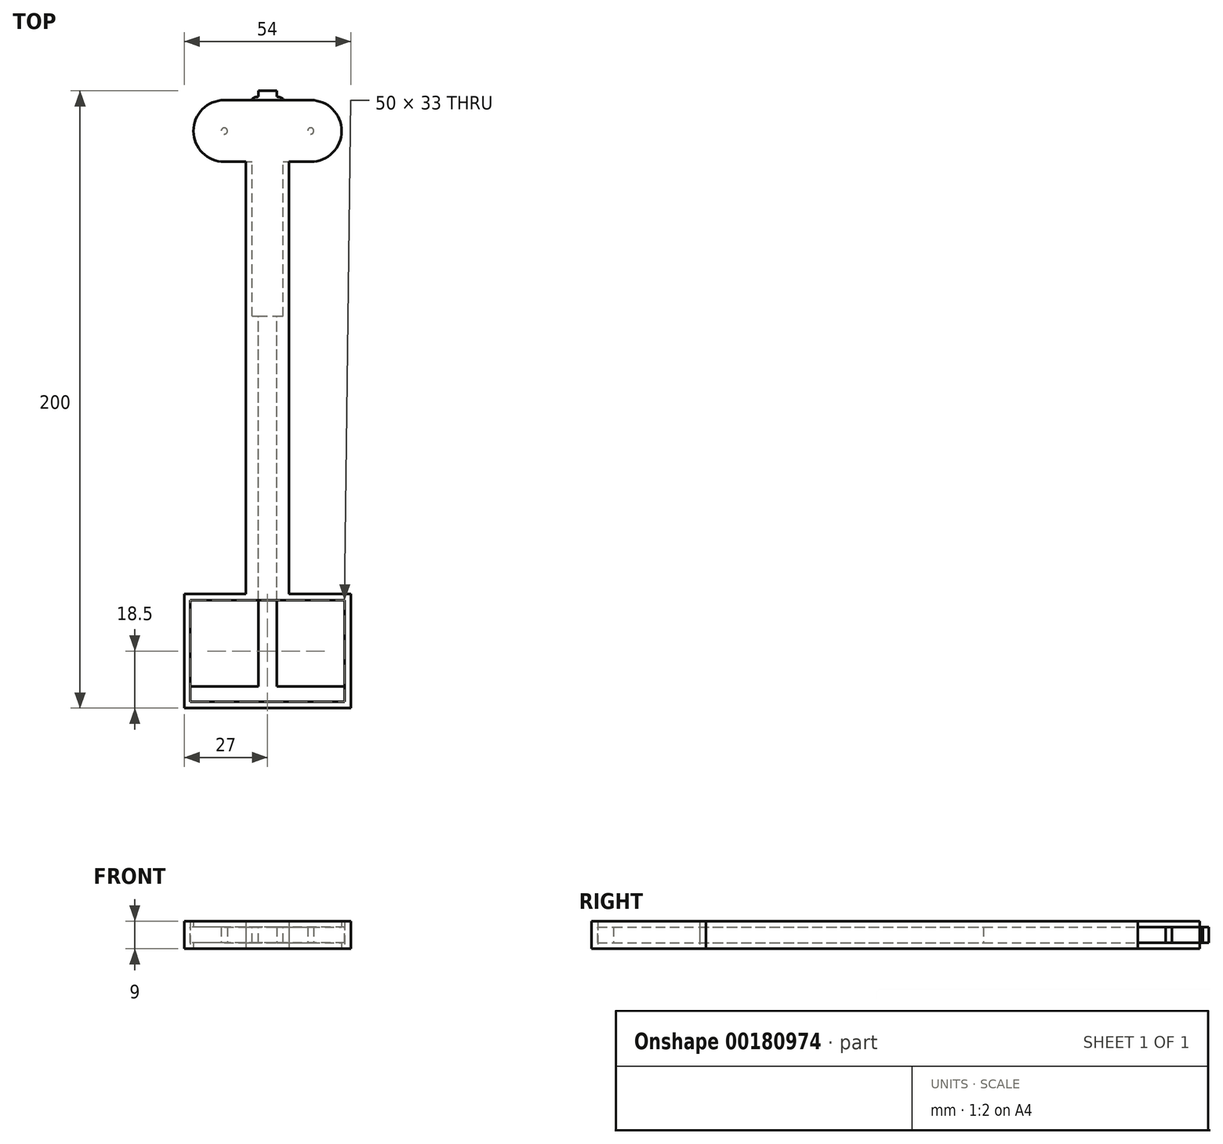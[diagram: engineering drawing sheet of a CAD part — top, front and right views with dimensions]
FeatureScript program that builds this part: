
annotation { "Feature Type Name" : "Feature", "Feature Type Description" : "" }
export const myFeature = defineFeature(function(context is Context, id is Id, definition is map)
    precondition{}
    {
        {
            var Q0;
            Q0=qCreatedBy(makeId("Top.planeOp"),FACE);
            var sketch = newSketch(context, id + "F0", { "sketchPlane" : qUnion([Q0])});
            skLineSegment(sketch, "E0.bottom", {"start": v(0, -180) * mm, "end": v(3, -180) * mm});
            skLineSegment(sketch, "E0.top", {"start": v(0, 13) * mm, "end": v(3, 13) * mm});
            skLineSegment(sketch, "E0.left", {"start": v(0, -180) * mm, "end": v(0, 13) * mm});
            skLineSegment(sketch, "E0.right", {"start": v(3, -180) * mm, "end": v(3, 13) * mm});
            skLineSegment(sketch, "E1", {"start": v(0, 10) * mm, "end": v(3, 10) * mm, "construction": true});
            skArc(sketch, "E2", {"start": v(3, 11.09) * mm, "mid": v(4.04, 10.94) * mm, "end": v(5, 10.5) * mm});
            skLineSegment(sketch, "E3", {"start": v(5, 10.5) * mm, "end": v(5, 10) * mm});
            skArc(sketch, "E4.MirrorCS", {"start": v(3, 8.91) * mm, "mid": v(4.04, 9.06) * mm, "end": v(5, 9.5) * mm});
            skLineSegment(sketch, "E5.MirrorCS", {"start": v(5, 9.5) * mm, "end": v(5, 10) * mm});
            skArc(sketch, "E6.1.0.0", {"start": v(3, 7.89) * mm, "mid": v(4.04, 7.74) * mm, "end": v(5, 7.3) * mm});
            skLineSegment(sketch, "E6.1.0.1", {"start": v(5, 7.3) * mm, "end": v(5, 6.8) * mm});
            skLineSegment(sketch, "E6.1.0.2", {"start": v(5, 6.3) * mm, "end": v(5, 6.8) * mm});
            skArc(sketch, "E6.1.0.3", {"start": v(3, 5.71) * mm, "mid": v(4.04, 5.86) * mm, "end": v(5, 6.3) * mm});
            skArc(sketch, "E6.2.0.0", {"start": v(3, 4.69) * mm, "mid": v(4.04, 4.54) * mm, "end": v(5, 4.1) * mm});
            skLineSegment(sketch, "E6.2.0.1", {"start": v(5, 4.1) * mm, "end": v(5, 3.6) * mm});
            skLineSegment(sketch, "E6.2.0.2", {"start": v(5, 3.1) * mm, "end": v(5, 3.6) * mm});
            skArc(sketch, "E6.2.0.3", {"start": v(3, 2.51) * mm, "mid": v(4.04, 2.66) * mm, "end": v(5, 3.1) * mm});
            skLineSegment(sketch, "E6.direction1", {"start": v(3, 7.39) * mm, "end": v(3, 4.19) * mm, "construction": true});
            skArc(sketch, "E7.0.3.0", {"start": v(3, 1.49) * mm, "mid": v(4.04, 1.34) * mm, "end": v(5, 0.9) * mm});
            skLineSegment(sketch, "E7.4.3.0", {"start": v(5, 0.9) * mm, "end": v(5, 0.4) * mm});
            skLineSegment(sketch, "E7.7.3.0", {"start": v(5, -0.1) * mm, "end": v(5, 0.4) * mm});
            skArc(sketch, "E7.10.3.0", {"start": v(3, -0.69) * mm, "mid": v(4.04, -0.54) * mm, "end": v(5, -0.1) * mm});
            skArc(sketch, "E7.0.4.0", {"start": v(3, -1.71) * mm, "mid": v(4.04, -1.86) * mm, "end": v(5, -2.3) * mm});
            skLineSegment(sketch, "E7.4.4.0", {"start": v(5, -2.3) * mm, "end": v(5, -2.8) * mm});
            skLineSegment(sketch, "E7.7.4.0", {"start": v(5, -3.3) * mm, "end": v(5, -2.8) * mm});
            skArc(sketch, "E7.10.4.0", {"start": v(3, -3.89) * mm, "mid": v(4.04, -3.74) * mm, "end": v(5, -3.3) * mm});
            skArc(sketch, "E7.0.5.0", {"start": v(3, -4.91) * mm, "mid": v(4.04, -5.06) * mm, "end": v(5, -5.5) * mm});
            skLineSegment(sketch, "E7.4.5.0", {"start": v(5, -5.5) * mm, "end": v(5, -6) * mm});
            skLineSegment(sketch, "E7.7.5.0", {"start": v(5, -6.5) * mm, "end": v(5, -6) * mm});
            skArc(sketch, "E7.10.5.0", {"start": v(3, -7.09) * mm, "mid": v(4.04, -6.94) * mm, "end": v(5, -6.5) * mm});
            skArc(sketch, "E7.0.6.0", {"start": v(3, -8.11) * mm, "mid": v(4.04, -8.26) * mm, "end": v(5, -8.7) * mm});
            skLineSegment(sketch, "E7.4.6.0", {"start": v(5, -8.7) * mm, "end": v(5, -9.2) * mm});
            skLineSegment(sketch, "E7.7.6.0", {"start": v(5, -9.7) * mm, "end": v(5, -9.2) * mm});
            skArc(sketch, "E7.10.6.0", {"start": v(3, -10.29) * mm, "mid": v(4.04, -10.14) * mm, "end": v(5, -9.7) * mm});
            skArc(sketch, "E7.0.7.0", {"start": v(3, -11.31) * mm, "mid": v(4.04, -11.46) * mm, "end": v(5, -11.9) * mm});
            skLineSegment(sketch, "E7.4.7.0", {"start": v(5, -11.9) * mm, "end": v(5, -12.4) * mm});
            skLineSegment(sketch, "E7.7.7.0", {"start": v(5, -12.9) * mm, "end": v(5, -12.4) * mm});
            skArc(sketch, "E7.10.7.0", {"start": v(3, -13.49) * mm, "mid": v(4.04, -13.34) * mm, "end": v(5, -12.9) * mm});
            skArc(sketch, "E7.0.8.0", {"start": v(3, -14.51) * mm, "mid": v(4.04, -14.66) * mm, "end": v(5, -15.1) * mm});
            skLineSegment(sketch, "E7.4.8.0", {"start": v(5, -15.1) * mm, "end": v(5, -15.6) * mm});
            skLineSegment(sketch, "E7.7.8.0", {"start": v(5, -16.1) * mm, "end": v(5, -15.6) * mm});
            skArc(sketch, "E7.10.8.0", {"start": v(3, -16.69) * mm, "mid": v(4.04, -16.54) * mm, "end": v(5, -16.1) * mm});
            skArc(sketch, "E7.0.9.0", {"start": v(3, -17.71) * mm, "mid": v(4.04, -17.86) * mm, "end": v(5, -18.3) * mm});
            skLineSegment(sketch, "E7.4.9.0", {"start": v(5, -18.3) * mm, "end": v(5, -18.8) * mm});
            skLineSegment(sketch, "E7.7.9.0", {"start": v(5, -19.3) * mm, "end": v(5, -18.8) * mm});
            skArc(sketch, "E7.10.9.0", {"start": v(3, -19.89) * mm, "mid": v(4.04, -19.74) * mm, "end": v(5, -19.3) * mm});
            skArc(sketch, "E7.0.10.0", {"start": v(3, -20.91) * mm, "mid": v(4.04, -21.06) * mm, "end": v(5, -21.5) * mm});
            skLineSegment(sketch, "E7.4.10.0", {"start": v(5, -21.5) * mm, "end": v(5, -22) * mm});
            skLineSegment(sketch, "E7.7.10.0", {"start": v(5, -22.5) * mm, "end": v(5, -22) * mm});
            skArc(sketch, "E7.10.10.0", {"start": v(3, -23.09) * mm, "mid": v(4.04, -22.94) * mm, "end": v(5, -22.5) * mm});
            skArc(sketch, "E7.0.11.0", {"start": v(3, -24.11) * mm, "mid": v(4.04, -24.26) * mm, "end": v(5, -24.7) * mm});
            skLineSegment(sketch, "E7.4.11.0", {"start": v(5, -24.7) * mm, "end": v(5, -25.2) * mm});
            skLineSegment(sketch, "E7.7.11.0", {"start": v(5, -25.7) * mm, "end": v(5, -25.2) * mm});
            skArc(sketch, "E7.10.11.0", {"start": v(3, -26.29) * mm, "mid": v(4.04, -26.14) * mm, "end": v(5, -25.7) * mm});
            skArc(sketch, "E7.0.12.0", {"start": v(3, -27.31) * mm, "mid": v(4.04, -27.46) * mm, "end": v(5, -27.9) * mm});
            skLineSegment(sketch, "E7.4.12.0", {"start": v(5, -27.9) * mm, "end": v(5, -28.4) * mm});
            skLineSegment(sketch, "E7.7.12.0", {"start": v(5, -28.9) * mm, "end": v(5, -28.4) * mm});
            skArc(sketch, "E7.10.12.0", {"start": v(3, -29.49) * mm, "mid": v(4.04, -29.34) * mm, "end": v(5, -28.9) * mm});
            skArc(sketch, "E7.0.13.0", {"start": v(3, -30.51) * mm, "mid": v(4.04, -30.66) * mm, "end": v(5, -31.1) * mm});
            skLineSegment(sketch, "E7.4.13.0", {"start": v(5, -31.1) * mm, "end": v(5, -31.6) * mm});
            skLineSegment(sketch, "E7.7.13.0", {"start": v(5, -32.1) * mm, "end": v(5, -31.6) * mm});
            skArc(sketch, "E7.10.13.0", {"start": v(3, -32.69) * mm, "mid": v(4.04, -32.54) * mm, "end": v(5, -32.1) * mm});
            skArc(sketch, "E7.0.14.0", {"start": v(3, -33.71) * mm, "mid": v(4.04, -33.86) * mm, "end": v(5, -34.3) * mm});
            skLineSegment(sketch, "E7.4.14.0", {"start": v(5, -34.3) * mm, "end": v(5, -34.8) * mm});
            skLineSegment(sketch, "E7.7.14.0", {"start": v(5, -35.3) * mm, "end": v(5, -34.8) * mm});
            skArc(sketch, "E7.10.14.0", {"start": v(3, -35.89) * mm, "mid": v(4.04, -35.74) * mm, "end": v(5, -35.3) * mm});
            skArc(sketch, "E7.0.15.0", {"start": v(3, -36.91) * mm, "mid": v(4.04, -37.06) * mm, "end": v(5, -37.5) * mm});
            skLineSegment(sketch, "E7.4.15.0", {"start": v(5, -37.5) * mm, "end": v(5, -38) * mm});
            skLineSegment(sketch, "E7.7.15.0", {"start": v(5, -38.5) * mm, "end": v(5, -38) * mm});
            skArc(sketch, "E7.10.15.0", {"start": v(3, -39.09) * mm, "mid": v(4.04, -38.94) * mm, "end": v(5, -38.5) * mm});
            skSolve(sketch);
        }
        {
            var Q0;
            Q0 = qSketchRegion(id + "F0", true);
            extrude(context, id + "F1", {"entities" : qUnion([Q0]), "depth" : 5 * mm});
        }
        {
            var Q0;
            Q0=makeQuery(id+"F1.opExtrude","SWEPT_BODY",BODY,{"disambiguationData":[OSD([sQuery(id+"F0.wireOp",EDGE,"E0.bottom"),sQuery(id+"F0.wireOp",EDGE,"E0.top"),sQuery(id+"F0.wireOp",EDGE,"E0.left"),sQuery(id+"F0.wireOp",EDGE,"E0.right"),sQuery(id+"F0.wireOp",EDGE,"E2"),sQuery(id+"F0.wireOp",EDGE,"E3"),sQuery(id+"F0.wireOp",EDGE,"E4.MirrorCS"),sQuery(id+"F0.wireOp",EDGE,"E5.MirrorCS"),sQuery(id+"F0.wireOp",EDGE,"E6.1.0.0"),sQuery(id+"F0.wireOp",EDGE,"E6.1.0.1"),sQuery(id+"F0.wireOp",EDGE,"E6.1.0.2"),sQuery(id+"F0.wireOp",EDGE,"E6.1.0.3"),sQuery(id+"F0.wireOp",EDGE,"E6.2.0.0"),sQuery(id+"F0.wireOp",EDGE,"E6.2.0.1"),sQuery(id+"F0.wireOp",EDGE,"E6.2.0.2"),sQuery(id+"F0.wireOp",EDGE,"E6.2.0.3"),sQuery(id+"F0.wireOp",EDGE,"E7.0.3.0"),sQuery(id+"F0.wireOp",EDGE,"E7.4.3.0"),sQuery(id+"F0.wireOp",EDGE,"E7.7.3.0"),sQuery(id+"F0.wireOp",EDGE,"E7.10.3.0"),sQuery(id+"F0.wireOp",EDGE,"E7.0.4.0"),sQuery(id+"F0.wireOp",EDGE,"E7.4.4.0"),sQuery(id+"F0.wireOp",EDGE,"E7.7.4.0"),sQuery(id+"F0.wireOp",EDGE,"E7.10.4.0"),sQuery(id+"F0.wireOp",EDGE,"E7.0.5.0"),sQuery(id+"F0.wireOp",EDGE,"E7.4.5.0"),sQuery(id+"F0.wireOp",EDGE,"E7.7.5.0"),sQuery(id+"F0.wireOp",EDGE,"E7.10.5.0"),sQuery(id+"F0.wireOp",EDGE,"E7.0.6.0"),sQuery(id+"F0.wireOp",EDGE,"E7.4.6.0"),sQuery(id+"F0.wireOp",EDGE,"E7.7.6.0"),sQuery(id+"F0.wireOp",EDGE,"E7.10.6.0"),sQuery(id+"F0.wireOp",EDGE,"E7.0.7.0"),sQuery(id+"F0.wireOp",EDGE,"E7.4.7.0"),sQuery(id+"F0.wireOp",EDGE,"E7.7.7.0"),sQuery(id+"F0.wireOp",EDGE,"E7.10.7.0"),sQuery(id+"F0.wireOp",EDGE,"E7.0.8.0"),sQuery(id+"F0.wireOp",EDGE,"E7.4.8.0"),sQuery(id+"F0.wireOp",EDGE,"E7.7.8.0"),sQuery(id+"F0.wireOp",EDGE,"E7.10.8.0"),sQuery(id+"F0.wireOp",EDGE,"E7.0.9.0"),sQuery(id+"F0.wireOp",EDGE,"E7.4.9.0"),sQuery(id+"F0.wireOp",EDGE,"E7.7.9.0"),sQuery(id+"F0.wireOp",EDGE,"E7.10.9.0"),sQuery(id+"F0.wireOp",EDGE,"E7.0.10.0"),sQuery(id+"F0.wireOp",EDGE,"E7.4.10.0"),sQuery(id+"F0.wireOp",EDGE,"E7.7.10.0"),sQuery(id+"F0.wireOp",EDGE,"E7.10.10.0"),sQuery(id+"F0.wireOp",EDGE,"E7.0.11.0"),sQuery(id+"F0.wireOp",EDGE,"E7.4.11.0"),sQuery(id+"F0.wireOp",EDGE,"E7.7.11.0"),sQuery(id+"F0.wireOp",EDGE,"E7.10.11.0"),sQuery(id+"F0.wireOp",EDGE,"E7.0.12.0"),sQuery(id+"F0.wireOp",EDGE,"E7.4.12.0"),sQuery(id+"F0.wireOp",EDGE,"E7.7.12.0"),sQuery(id+"F0.wireOp",EDGE,"E7.10.12.0"),sQuery(id+"F0.wireOp",EDGE,"E7.0.13.0"),sQuery(id+"F0.wireOp",EDGE,"E7.4.13.0"),sQuery(id+"F0.wireOp",EDGE,"E7.7.13.0"),sQuery(id+"F0.wireOp",EDGE,"E7.10.13.0"),sQuery(id+"F0.wireOp",EDGE,"E7.0.14.0"),sQuery(id+"F0.wireOp",EDGE,"E7.4.14.0"),sQuery(id+"F0.wireOp",EDGE,"E7.7.14.0"),sQuery(id+"F0.wireOp",EDGE,"E7.10.14.0"),sQuery(id+"F0.wireOp",EDGE,"E7.0.15.0"),sQuery(id+"F0.wireOp",EDGE,"E7.4.15.0"),sQuery(id+"F0.wireOp",EDGE,"E7.7.15.0"),sQuery(id+"F0.wireOp",EDGE,"E7.10.15.0")])]});
            var Q1;
            Q1=makeQuery(id+"F1.opExtrude","SWEPT_FACE",FACE,{"disambiguationData":[OSD([sQuery(id+"F0.wireOp",EDGE,"E0.left")])]});
            mirror(context, id + "F2", {"operationType" : NewBodyOperationType.ADD, "entities" : qUnion([Q0]), "mirrorPlane" : qUnion([Q1])});
        }
        {
            var Q0;
            {var subQ0=makeQuery(id+"F1.opExtrude","SWEPT_FACE",FACE,{"disambiguationData":[OSD([sQuery(id+"F0.wireOp",EDGE,"E0.bottom")])]});Q0=makeQuery(id+"F2.boolean.opBoolean","MERGE",FACE,{"derivedFrom":[subQ0,makeQuery(id+"F2.opPattern","COPY",FACE,{"derivedFrom":subQ0,"instanceName":"1"})]});}
            var sketch = newSketch(context, id + "F3", { "sketchPlane" : qUnion([Q0])});
            skLineSegment(sketch, "E8.bottom", {"start": v(25, 0) * mm, "end": v(-25, 0) * mm});
            skLineSegment(sketch, "E8.top", {"start": v(25, 5) * mm, "end": v(-25, 5) * mm});
            skLineSegment(sketch, "E8.left", {"start": v(25, 0) * mm, "end": v(25, 5) * mm});
            skLineSegment(sketch, "E8.right", {"start": v(-25, 0) * mm, "end": v(-25, 5) * mm});
            skPoint(sketch, "E8.middle", {"position": v(0, 2.5) * mm});
            skPoint(sketch, "E8.middle.positionSnap0", {"position": v(-3, 2.5) * mm});
            skPoint(sketch, "E8.centerSnap0", {"position": v(-3, 2.5) * mm});
            skSolve(sketch);
        }
        {
            var Q0;
            Q0 = qSketchRegion(id + "F3", true);
            extrude(context, id + "F4", {"entities" : qUnion([Q0]), "operationType" : NewBodyOperationType.ADD, "depth" : 5 * mm});
        }
        {
            var Q0;
            Q0=qCreatedBy(makeId("Top.planeOp"),FACE);
            var sketch = newSketch(context, id + "F5", { "sketchPlane" : qUnion([Q0])});
            skCircle(sketch, "E9", {"center": v(14, 0) * mm, "radius": 10 * mm});
            skLineSegment(sketch, "E10", {"start": v(0, 10) * mm, "end": v(14, 10) * mm});
            skLineSegment(sketch, "E11", {"start": v(0, -187) * mm, "end": v(27, -187) * mm});
            skLineSegment(sketch, "E12", {"start": v(27, -187) * mm, "end": v(27, -150) * mm});
            skLineSegment(sketch, "E13", {"start": v(27, -150) * mm, "end": v(7, -150) * mm});
            skLineSegment(sketch, "E14", {"start": v(7, -150) * mm, "end": v(7, -10) * mm});
            skLineSegment(sketch, "E15", {"start": v(7, -10) * mm, "end": v(14, -10) * mm});
            skLineSegment(sketch, "E16.MirrorCS", {"start": v(0, 10) * mm, "end": v(-14, 10) * mm});
            skCircle(sketch, "E17.MirrorC", {"center": v(-14, 0) * mm, "radius": 10 * mm});
            skLineSegment(sketch, "E18.MirrorCS", {"start": v(-7, -10) * mm, "end": v(-14, -10) * mm});
            skLineSegment(sketch, "E19.MirrorCS", {"start": v(-7, -150) * mm, "end": v(-7, -10) * mm});
            skLineSegment(sketch, "E20.MirrorCS", {"start": v(-27, -150) * mm, "end": v(-7, -150) * mm});
            skLineSegment(sketch, "E21.MirrorCS", {"start": v(-27, -187) * mm, "end": v(-27, -150) * mm});
            skLineSegment(sketch, "E22.MirrorCS", {"start": v(0, -187) * mm, "end": v(-27, -187) * mm});
            skLineSegment(sketch, "E23.bottom", {"start": v(25, -185) * mm, "end": v(-25, -185) * mm});
            skLineSegment(sketch, "E23.top", {"start": v(25, -152) * mm, "end": v(-25, -152) * mm});
            skLineSegment(sketch, "E23.left", {"start": v(25, -185) * mm, "end": v(25, -152) * mm});
            skLineSegment(sketch, "E23.right", {"start": v(-25, -185) * mm, "end": v(-25, -152) * mm});
            skPoint(sketch, "E23.middle", {"position": v(0, -168.5) * mm});
            skSolve(sketch);
        }
        {
            var Q0;
            Q0 = qSketchRegion(id + "F5", true);
            extrude(context, id + "F6", {"entities" : qUnion([Q0]), "depth" : 7 * mm, "hasSecondDirection" : true, "secondDirectionOppositeDirection" : true, "secondDirectionDepth" : 2 * mm});
        }
        {
            var Q0;
            Q0=makeQuery(id+"F1.opExtrude","SWEPT_BODY",BODY,{"disambiguationData":[OSD([sQuery(id+"F0.wireOp",EDGE,"E0.bottom"),sQuery(id+"F0.wireOp",EDGE,"E0.top"),sQuery(id+"F0.wireOp",EDGE,"E0.left"),sQuery(id+"F0.wireOp",EDGE,"E0.right"),sQuery(id+"F0.wireOp",EDGE,"E2"),sQuery(id+"F0.wireOp",EDGE,"E3"),sQuery(id+"F0.wireOp",EDGE,"E4.MirrorCS"),sQuery(id+"F0.wireOp",EDGE,"E5.MirrorCS"),sQuery(id+"F0.wireOp",EDGE,"E6.1.0.0"),sQuery(id+"F0.wireOp",EDGE,"E6.1.0.1"),sQuery(id+"F0.wireOp",EDGE,"E6.1.0.2"),sQuery(id+"F0.wireOp",EDGE,"E6.1.0.3"),sQuery(id+"F0.wireOp",EDGE,"E6.2.0.0"),sQuery(id+"F0.wireOp",EDGE,"E6.2.0.1"),sQuery(id+"F0.wireOp",EDGE,"E6.2.0.2"),sQuery(id+"F0.wireOp",EDGE,"E6.2.0.3"),sQuery(id+"F0.wireOp",EDGE,"E7.0.3.0"),sQuery(id+"F0.wireOp",EDGE,"E7.4.3.0"),sQuery(id+"F0.wireOp",EDGE,"E7.7.3.0"),sQuery(id+"F0.wireOp",EDGE,"E7.10.3.0"),sQuery(id+"F0.wireOp",EDGE,"E7.0.4.0"),sQuery(id+"F0.wireOp",EDGE,"E7.4.4.0"),sQuery(id+"F0.wireOp",EDGE,"E7.7.4.0"),sQuery(id+"F0.wireOp",EDGE,"E7.10.4.0"),sQuery(id+"F0.wireOp",EDGE,"E7.0.5.0"),sQuery(id+"F0.wireOp",EDGE,"E7.4.5.0"),sQuery(id+"F0.wireOp",EDGE,"E7.7.5.0"),sQuery(id+"F0.wireOp",EDGE,"E7.10.5.0"),sQuery(id+"F0.wireOp",EDGE,"E7.0.6.0"),sQuery(id+"F0.wireOp",EDGE,"E7.4.6.0"),sQuery(id+"F0.wireOp",EDGE,"E7.7.6.0"),sQuery(id+"F0.wireOp",EDGE,"E7.10.6.0"),sQuery(id+"F0.wireOp",EDGE,"E7.0.7.0"),sQuery(id+"F0.wireOp",EDGE,"E7.4.7.0"),sQuery(id+"F0.wireOp",EDGE,"E7.7.7.0"),sQuery(id+"F0.wireOp",EDGE,"E7.10.7.0"),sQuery(id+"F0.wireOp",EDGE,"E7.0.8.0"),sQuery(id+"F0.wireOp",EDGE,"E7.4.8.0"),sQuery(id+"F0.wireOp",EDGE,"E7.7.8.0"),sQuery(id+"F0.wireOp",EDGE,"E7.10.8.0"),sQuery(id+"F0.wireOp",EDGE,"E7.0.9.0"),sQuery(id+"F0.wireOp",EDGE,"E7.4.9.0"),sQuery(id+"F0.wireOp",EDGE,"E7.7.9.0"),sQuery(id+"F0.wireOp",EDGE,"E7.10.9.0"),sQuery(id+"F0.wireOp",EDGE,"E7.0.10.0"),sQuery(id+"F0.wireOp",EDGE,"E7.4.10.0"),sQuery(id+"F0.wireOp",EDGE,"E7.7.10.0"),sQuery(id+"F0.wireOp",EDGE,"E7.10.10.0"),sQuery(id+"F0.wireOp",EDGE,"E7.0.11.0"),sQuery(id+"F0.wireOp",EDGE,"E7.4.11.0"),sQuery(id+"F0.wireOp",EDGE,"E7.7.11.0"),sQuery(id+"F0.wireOp",EDGE,"E7.10.11.0"),sQuery(id+"F0.wireOp",EDGE,"E7.0.12.0"),sQuery(id+"F0.wireOp",EDGE,"E7.4.12.0"),sQuery(id+"F0.wireOp",EDGE,"E7.7.12.0"),sQuery(id+"F0.wireOp",EDGE,"E7.10.12.0"),sQuery(id+"F0.wireOp",EDGE,"E7.0.13.0"),sQuery(id+"F0.wireOp",EDGE,"E7.4.13.0"),sQuery(id+"F0.wireOp",EDGE,"E7.7.13.0"),sQuery(id+"F0.wireOp",EDGE,"E7.10.13.0"),sQuery(id+"F0.wireOp",EDGE,"E7.0.14.0"),sQuery(id+"F0.wireOp",EDGE,"E7.4.14.0"),sQuery(id+"F0.wireOp",EDGE,"E7.7.14.0"),sQuery(id+"F0.wireOp",EDGE,"E7.10.14.0"),sQuery(id+"F0.wireOp",EDGE,"E7.0.15.0"),sQuery(id+"F0.wireOp",EDGE,"E7.4.15.0"),sQuery(id+"F0.wireOp",EDGE,"E7.7.15.0"),sQuery(id+"F0.wireOp",EDGE,"E7.10.15.0")])]});
            var Q1;
            Q1=makeQuery(id+"F6.opExtrude","SWEPT_BODY",BODY,{"disambiguationData":[OSD([sQuery(id+"F5.wireOp",EDGE,"E9"),sQuery(id+"F5.wireOp",EDGE,"E10"),sQuery(id+"F5.wireOp",EDGE,"E11"),sQuery(id+"F5.wireOp",EDGE,"E12"),sQuery(id+"F5.wireOp",EDGE,"E13"),sQuery(id+"F5.wireOp",EDGE,"E14"),sQuery(id+"F5.wireOp",EDGE,"E15"),sQuery(id+"F5.wireOp",EDGE,"E16.MirrorCS"),sQuery(id+"F5.wireOp",EDGE,"E17.MirrorC"),sQuery(id+"F5.wireOp",EDGE,"E18.MirrorCS"),sQuery(id+"F5.wireOp",EDGE,"E19.MirrorCS"),sQuery(id+"F5.wireOp",EDGE,"E20.MirrorCS"),sQuery(id+"F5.wireOp",EDGE,"E21.MirrorCS"),sQuery(id+"F5.wireOp",EDGE,"E22.MirrorCS"),sQuery(id+"F5.wireOp",EDGE,"E23.bottom"),sQuery(id+"F5.wireOp",EDGE,"E23.top"),sQuery(id+"F5.wireOp",EDGE,"E23.left"),sQuery(id+"F5.wireOp",EDGE,"E23.right")])]});
            booleanBodies(context, id + "F7", {"operationType" : BooleanOperationType.SUBTRACTION, "tools" : qUnion([Q0]), "targets" : qUnion([Q1]), "keepTools" : true});
        }
        {
            var Q0;
            Q0=qCreatedBy(makeId("Top.planeOp"),FACE);
            var sketch = newSketch(context, id + "F8", { "sketchPlane" : qUnion([Q0])});
            skArc(sketch, "E24.0", {"start": v(-14, -10) * mm, "mid": v(-24, 0) * mm, "end": v(-14, 10) * mm});
            skLineSegment(sketch, "E25.0", {"start": v(-14, 10) * mm, "end": v(14, 10) * mm});
            skArc(sketch, "E26.0", {"start": v(14, -10) * mm, "mid": v(24, 0) * mm, "end": v(14, 10) * mm});
            skLineSegment(sketch, "E27", {"start": v(-14, -10) * mm, "end": v(14, -10) * mm});
            skSolve(sketch);
        }
        {
            var Q0;
            Q0 = qSketchRegion(id + "F8", true);
            extrude(context, id + "F9", {"entities" : qUnion([Q0]), "operationType" : NewBodyOperationType.REMOVE, "depth" : 5 * mm});
        }
        {
            var Q0;
            {var subQ69=sQuery(id+"F8.wireOp",EDGE,"E27");Q0=makeQuery(id+"F9.boolean.opBoolean","COPY",FACE,{"disambiguationData":[TD([makeQuery(id+"F6.opExtrude","SWEPT_FACE",FACE,{"disambiguationData":[OSD([sQuery(id+"F5.wireOp",EDGE,"E18.MirrorCS")])]})])],"derivedFrom":makeQuery(id+"F9.opExtrude","SWEPT_FACE",FACE,{"disambiguationData":[OSD([subQ69])]})});}
            var sketch = newSketch(context, id + "F10", { "sketchPlane" : qUnion([Q0])});
            skLineSegment(sketch, "E28.bottom", {"start": v(5, 0) * mm, "end": v(-5, 0) * mm});
            skLineSegment(sketch, "E28.top", {"start": v(5, 5) * mm, "end": v(-5, 5) * mm});
            skLineSegment(sketch, "E28.left", {"start": v(5, 0) * mm, "end": v(5, 5) * mm});
            skLineSegment(sketch, "E28.right", {"start": v(-5, 0) * mm, "end": v(-5, 5) * mm});
            skSolve(sketch);
        }
        {
            var Q0;
            Q0 = qSketchRegion(id + "F10", true);
            extrude(context, id + "F11", {"entities" : qUnion([Q0]), "operationType" : NewBodyOperationType.REMOVE, "oppositeDirection" : true, "depth" : 50 * mm});
        }
        {
            var Q0;
            Q0=qCreatedBy(makeId("Top.planeOp"),FACE);
            var sketch = newSketch(context, id + "F12", { "sketchPlane" : qUnion([Q0])});
            skCircle(sketch, "E29", {"center": v(-14, 0) * mm, "radius": 1 * mm});
            skCircle(sketch, "E30", {"center": v(14, 0) * mm, "radius": 1 * mm});
            skSolve(sketch);
        }
        {
            var Q0;
            Q0 = qSketchRegion(id + "F12", true);
            extrude(context, id + "F13", {"entities" : qUnion([Q0]), "operationType" : NewBodyOperationType.ADD, "endBound" : BoundingType.UP_TO_NEXT, "depth" : 25 * mm});
        }
    });
